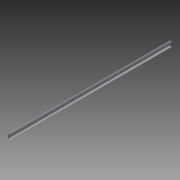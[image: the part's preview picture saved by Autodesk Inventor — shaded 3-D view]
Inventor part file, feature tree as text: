
AUTODESK INVENTOR PART (.ipt)
format: ipt  version: 2015 (Build 190159000, 159)  size: 147,456 bytes
history: native  units: in
note: dims shown in document units (in); Inventor stores cm internally (conversion verified against a paired STEP export)
features: other x3, sketch x2
ambient origin geometry x8: Origin, YZ Plane, XZ Plane, XY Plane, X Axis, Y Axis, Z Axis, Center Point
bodies: Solid1 (feature_tree)
feature tree (5):
  other  "garage door 2in rail.ipt"
  other  "Solid1::garage door 2in rail.ipt"
  other  "TaggingFeature1"
  sketch  "Sketch1"  dims[d0=0.3937in]
  sketch  "Sketch2"
